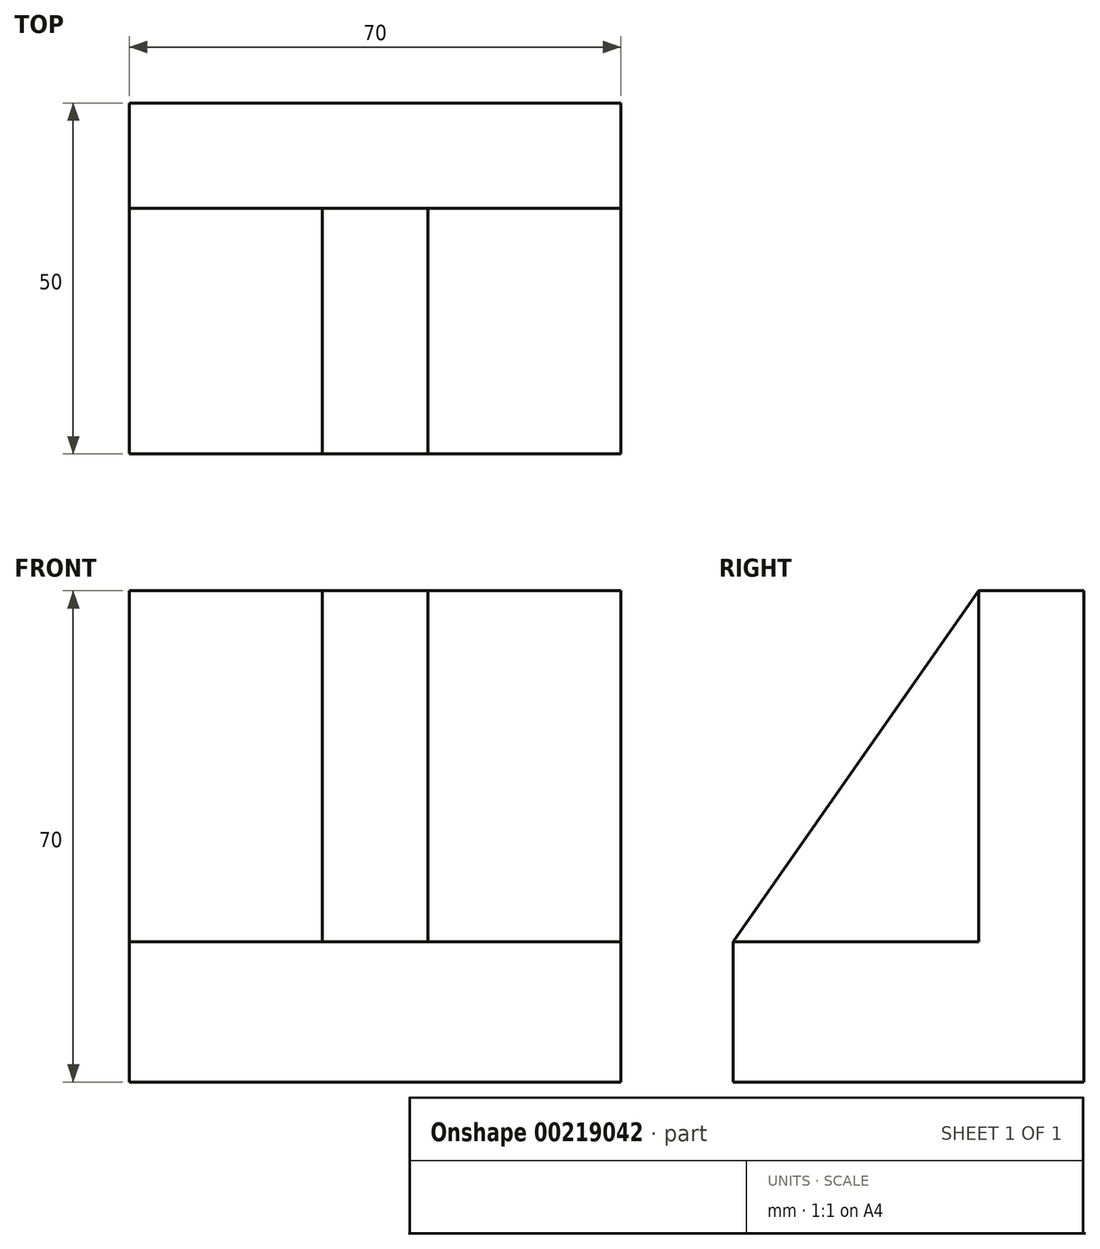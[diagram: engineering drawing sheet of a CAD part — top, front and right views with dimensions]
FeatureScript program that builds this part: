
annotation { "Feature Type Name" : "Feature", "Feature Type Description" : "" }
export const myFeature = defineFeature(function(context is Context, id is Id, definition is map)
    precondition{}
    {
        {
            var Q0;
            Q0=qCreatedBy(makeId("Top.planeOp"),FACE);
            var sketch = newSketch(context, id + "F0", { "sketchPlane" : qUnion([Q0])});
            skLineSegment(sketch, "E0.bottom", {"start": v(-35, -10) * mm, "end": v(35, -10) * mm});
            skLineSegment(sketch, "E0.top", {"start": v(-35, -60) * mm, "end": v(35, -60) * mm});
            skLineSegment(sketch, "E0.left", {"start": v(-35, -10) * mm, "end": v(-35, -60) * mm});
            skLineSegment(sketch, "E0.right", {"start": v(35, -10) * mm, "end": v(35, -60) * mm});
            skLineSegment(sketch, "E1", {"start": v(-35, -25) * mm, "end": v(35, -25) * mm});
            skSolve(sketch);
        }
        {
            var Q0;
            {var subQ0=sQuery(id+"F0.wireOp",EDGE,"E0.top");Q0=makeQuery(id+"F0.imprint","IMPRINT",FACE,{"disambiguationData":[TD([[makeQuery(id+"F0.imprint","IMPRINT",EDGE,{"derivedFrom":subQ0}),1.0]])]});}
            extrude(context, id + "F1", {"entities" : qUnion([Q0]), "depth" : 20 * mm});
        }
        {
            var Q0;
            {var subQ0=sQuery(id+"F0.wireOp",EDGE,"E0.bottom");Q0=makeQuery(id+"F0.imprint","IMPRINT",FACE,{"disambiguationData":[TD([[makeQuery(id+"F0.imprint","IMPRINT",EDGE,{"derivedFrom":subQ0}),-1.0]])]});}
            extrude(context, id + "F2", {"entities" : qUnion([Q0]), "operationType" : NewBodyOperationType.ADD, "depth" : 70 * mm});
        }
        {
            var Q0;
            Q0=qCreatedBy(makeId("Right.planeOp"),FACE);
            var sketch = newSketch(context, id + "F3", { "sketchPlane" : qUnion([Q0])});
            skLineSegment(sketch, "E2.0", {"start": v(-25, 70) * mm, "end": v(-25, 20) * mm});
            skLineSegment(sketch, "E3.0", {"start": v(-25, 20) * mm, "end": v(-60, 20) * mm});
            skLineSegment(sketch, "E4", {"start": v(-25, 70) * mm, "end": v(-60, 20) * mm});
            skSolve(sketch);
        }
        {
            var Q0;
            Q0 = qSketchRegion(id + "F3", true);
            extrude(context, id + "F4", {"entities" : qUnion([Q0]), "operationType" : NewBodyOperationType.ADD, "endBound" : BoundingType.SYMMETRIC, "depth" : 15 * mm});
        }
    });
